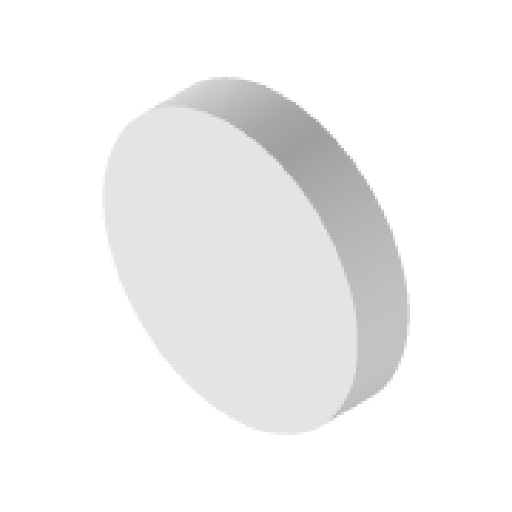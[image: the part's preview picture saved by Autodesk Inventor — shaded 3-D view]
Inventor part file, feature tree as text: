
AUTODESK INVENTOR PART (.ipt)
format: ipt  version: 2023 (Build 270158000, 158)  size: 82,432 bytes
history: native  units: in
note: dims shown in document units (in); Inventor stores cm internally (conversion verified against a paired STEP export)
features: extrude x1, sketch x1
ambient origin geometry x8: Origin, YZ Plane, XZ Plane, XY Plane, X Axis, Y Axis, Z Axis, Center Point
bodies: Solid1 (feature_tree)
feature tree (2):
  extrude  "Extrusion1"  Depth=0.1969in TaperAngle=0.0deg
  sketch  "Sketch1"  dims[d0=0.9843in d1=0.1969in d2=0.0in]
